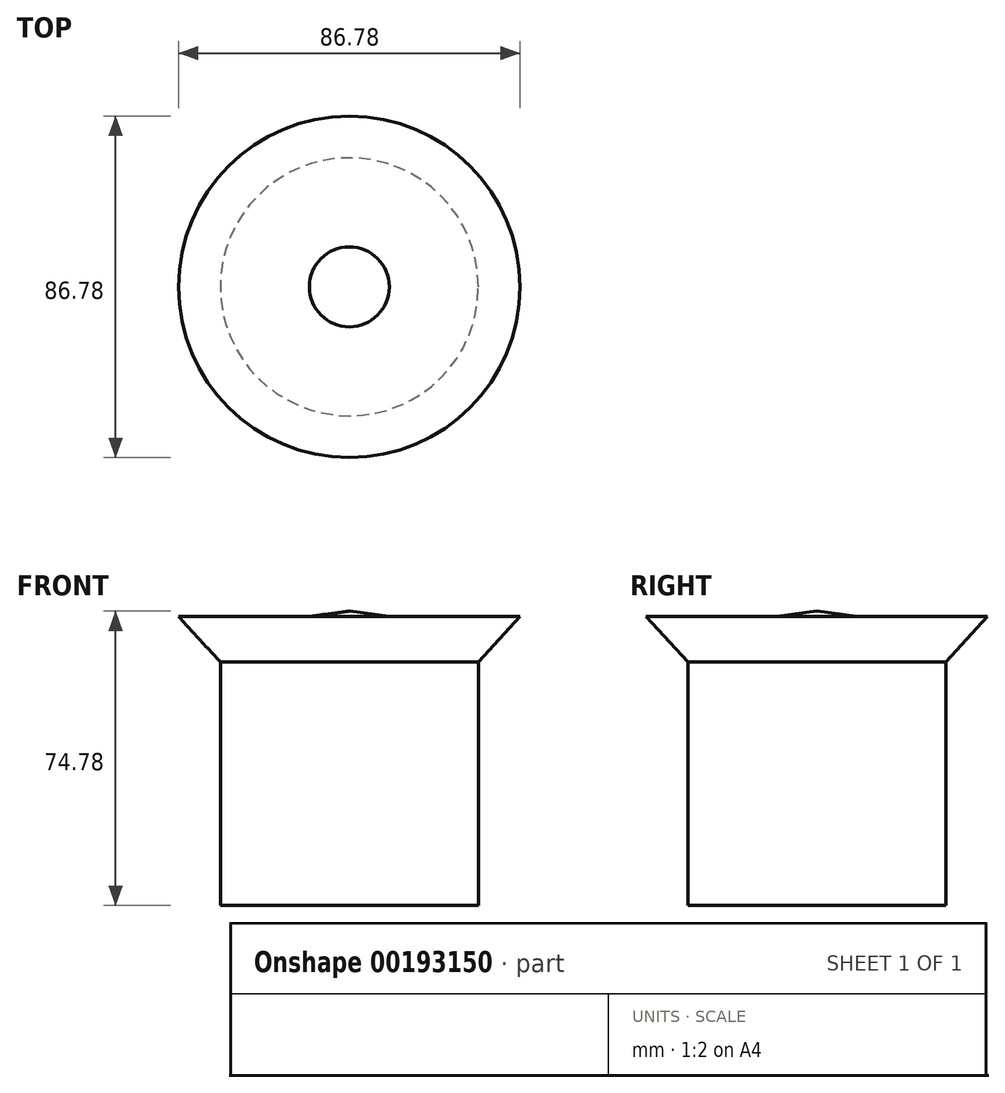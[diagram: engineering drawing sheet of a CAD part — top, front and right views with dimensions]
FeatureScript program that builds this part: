
annotation { "Feature Type Name" : "Feature", "Feature Type Description" : "" }
export const myFeature = defineFeature(function(context is Context, id is Id, definition is map)
    precondition{}
    {
        {
            var Q0;
            Q0=qCreatedBy(makeId("Front.planeOp"),FACE);
            var sketch = newSketch(context, id + "F0", { "sketchPlane" : qUnion([Q0])});
            skLineSegment(sketch, "E0", {"start": v(10.16, 44.08) * mm, "end": v(43.4, 44.08) * mm});
            skLineSegment(sketch, "E1", {"start": v(43.4, 44.08) * mm, "end": v(32.77, 32.54) * mm});
            skLineSegment(sketch, "E2", {"start": v(32.77, 32.54) * mm, "end": v(32.77, -29.31) * mm});
            skLineSegment(sketch, "E3", {"start": v(32.77, -29.31) * mm, "end": v(0, -29.31) * mm});
            skLineSegment(sketch, "E4", {"start": v(0, -29.31) * mm, "end": v(0, 45.47) * mm});
            skLineSegment(sketch, "E5", {"start": v(0, 45.47) * mm, "end": v(10.16, 44.08) * mm});
            skSolve(sketch);
        }
        {
            var Q0;
            Q0=makeQuery(id+"F0.imprint","IMPRINT",FACE,{"disambiguationData":[TD([[makeQuery(id+"F0.imprint","IMPRINT",EDGE,{"derivedFrom":sQuery(id+"F0.wireOp",EDGE,"E0")}),-1.0]])]});
            var Q1;
            Q1=sQuery(id+"F0.wireOp",EDGE,"E4");
            revolve(context, id + "F1", {"entities" : qUnion([Q0]), "axis" : qUnion([Q1]), "revolveType" : RevolveType.FULL});
        }
    });
